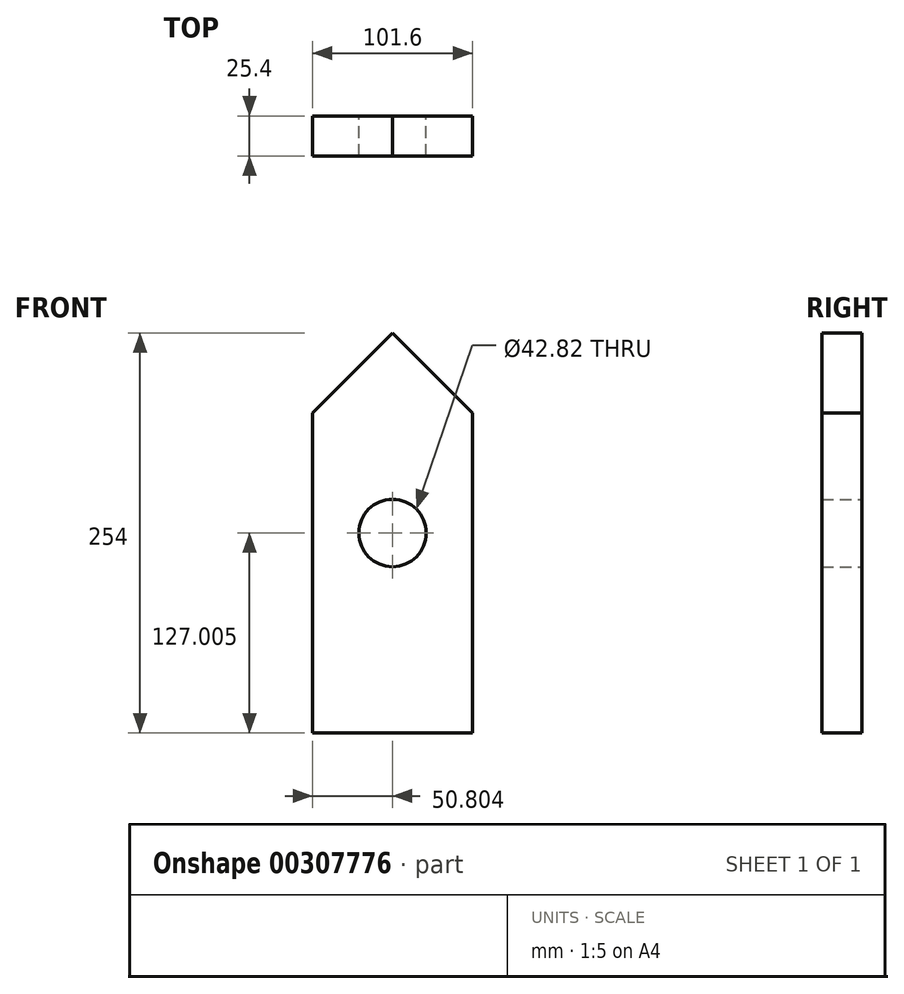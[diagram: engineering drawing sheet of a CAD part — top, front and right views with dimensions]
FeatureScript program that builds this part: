
annotation { "Feature Type Name" : "Feature", "Feature Type Description" : "" }
export const myFeature = defineFeature(function(context is Context, id is Id, definition is map)
    precondition{}
    {
        {
            var Q0;
            Q0=qCreatedBy(makeId("Front.planeOp"),FACE);
            var sketch = newSketch(context, id + "F0", { "sketchPlane" : qUnion([Q0])});
            skLineSegment(sketch, "E0.bottom", {"start": v(-96.43, 106.48) * mm, "end": v(5.17, 106.48) * mm});
            skLineSegment(sketch, "E0.top", {"start": v(-96.43, -96.72) * mm, "end": v(5.17, -96.72) * mm});
            skLineSegment(sketch, "E0.left", {"start": v(-96.43, 106.48) * mm, "end": v(-96.43, -96.72) * mm});
            skLineSegment(sketch, "E0.right", {"start": v(5.17, 106.48) * mm, "end": v(5.17, -96.72) * mm});
            skLineSegment(sketch, "E1", {"start": v(-96.43, 106.48) * mm, "end": v(-45.63, 157.28) * mm});
            skLineSegment(sketch, "E2", {"start": v(-45.63, 157.28) * mm, "end": v(5.17, 106.48) * mm});
            skCircle(sketch, "E3", {"center": v(-45.63, 30.28) * mm, "radius": 21.41 * mm});
            skSolve(sketch);
        }
        {
            var Q0;
            Q0=makeQuery(id+"F0.imprint","IMPRINT",FACE,{"disambiguationData":[TD([[makeQuery(id+"F0.imprint","IMPRINT",EDGE,{"derivedFrom":sQuery(id+"F0.wireOp",EDGE,"E0.bottom")}),-1.0]])]});
            var Q1;
            Q1=makeQuery(id+"F0.imprint","IMPRINT",FACE,{"disambiguationData":[TD([[makeQuery(id+"F0.imprint","IMPRINT",EDGE,{"derivedFrom":sQuery(id+"F0.wireOp",EDGE,"E0.bottom")}),1.0]])]});
            extrude(context, id + "F1", {"entities" : qUnion([Q0, Q1]), "depth" : 25.4 * mm});
        }
    });
